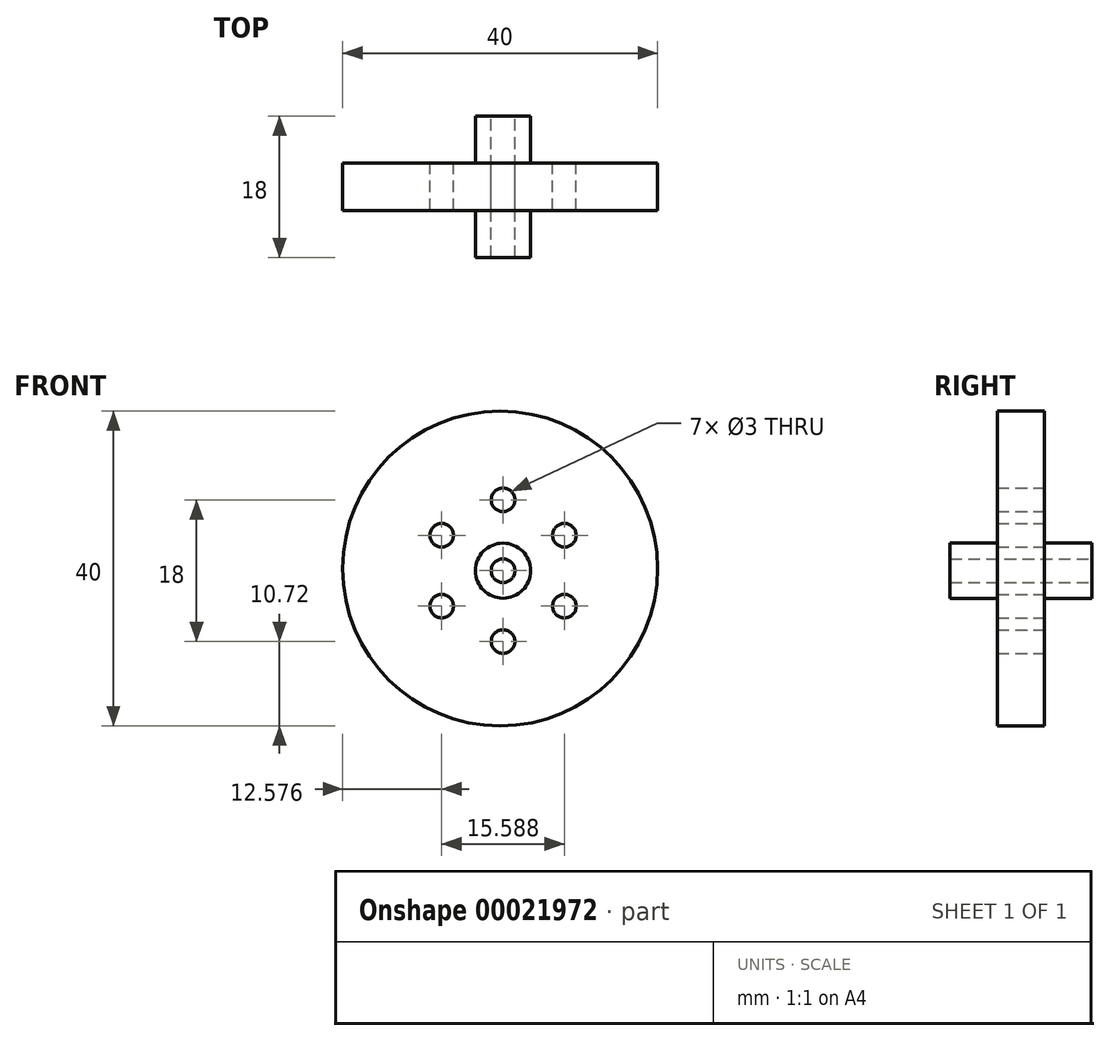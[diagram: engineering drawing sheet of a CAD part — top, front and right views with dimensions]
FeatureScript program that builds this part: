
annotation { "Feature Type Name" : "Feature", "Feature Type Description" : "" }
export const myFeature = defineFeature(function(context is Context, id is Id, definition is map)
    precondition{}
    {
        {
            var Q0;
            Q0=qCreatedBy(makeId("Front.planeOp"),FACE);
            var sketch = newSketch(context, id + "F0", { "sketchPlane" : qUnion([Q0])});
            skCircle(sketch, "E0", {"center": v(-0.37, 0.28) * mm, "radius": 20 * mm});
            skCircle(sketch, "E1", {"center": v(0, 0) * mm, "radius": 3.5 * mm});
            skCircle(sketch, "E2", {"center": v(0, 0) * mm, "radius": 1.5 * mm});
            skLineSegment(sketch, "E3", {"start": v(0, 1.5) * mm, "end": v(0, 9) * mm});
            skCircle(sketch, "E4", {"center": v(0, 9) * mm, "radius": 1.5 * mm});
            skCircle(sketch, "E5.1.0", {"center": v(-7.8, 4.5) * mm, "radius": 1.5 * mm});
            skCircle(sketch, "E5.2.0", {"center": v(-7.8, -4.5) * mm, "radius": 1.5 * mm});
            skCircle(sketch, "E5.3.0", {"center": v(0, -9) * mm, "radius": 1.5 * mm});
            skCircle(sketch, "E5.4.0", {"center": v(7.8, -4.5) * mm, "radius": 1.5 * mm});
            skCircle(sketch, "E5.5.0", {"center": v(7.8, 4.5) * mm, "radius": 1.5 * mm});
            skSolve(sketch);
        }
        {
            var Q0;
            Q0=makeQuery(id+"F0.imprint","IMPRINT",FACE,{"disambiguationData":[TD([[makeQuery(id+"F0.imprint","IMPRINT",EDGE,{"derivedFrom":sQuery(id+"F0.wireOp",EDGE,"E0")}),1.0]])]});
            var Q1;
            Q1=makeQuery(id+"F0.imprint","IMPRINT",FACE,{"disambiguationData":[TD([[makeQuery(id+"F0.imprint","IMPRINT",EDGE,{"derivedFrom":sQuery(id+"F0.wireOp",EDGE,"E1")}),1.0]])]});
            extrude(context, id + "F1", {"entities" : qUnion([Q0, Q1]), "depth" : 6 * mm});
        }
        {
            var Q0;
            Q0=makeQuery(id+"F0.imprint","IMPRINT",FACE,{"disambiguationData":[TD([[makeQuery(id+"F0.imprint","IMPRINT",EDGE,{"derivedFrom":sQuery(id+"F0.wireOp",EDGE,"E1")}),1.0]])]});
            extrude(context, id + "F2", {"entities" : qUnion([Q0]), "operationType" : NewBodyOperationType.ADD, "depth" : 12 * mm});
        }
        {
            var Q0;
            Q0=makeQuery(id+"F0.imprint","IMPRINT",FACE,{"disambiguationData":[TD([[makeQuery(id+"F0.imprint","IMPRINT",EDGE,{"derivedFrom":sQuery(id+"F0.wireOp",EDGE,"E1")}),1.0]])]});
            extrude(context, id + "F3", {"entities" : qUnion([Q0]), "operationType" : NewBodyOperationType.ADD, "depth" : 6 * mm, "hasSecondDirection" : true, "secondDirectionOppositeDirection" : true, "secondDirectionDepth" : 6 * mm});
        }
    });
